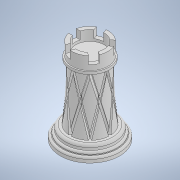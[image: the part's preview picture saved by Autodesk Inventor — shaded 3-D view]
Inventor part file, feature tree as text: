
AUTODESK INVENTOR PART (.ipt)
format: ipt  version: 2022 (Build 260153000, 153)  size: 847,872 bytes
history: native  units: mm
features: other x5, sketch x5, pattern_circular x3, loft x2, projected_geometry x2, revolve x1, extrude x1, fillet x1
ambient origin geometry x8: Origin, YZ Plane, XZ Plane, XY Plane, X Axis, Y Axis, Z Axis, Center Point
bodies: Solid1 (feature_tree)
feature tree (20):
  other  "Back Line Base.ipt"
  revolve  "Revolution1"  [1 undecoded]
  extrude  "Extrusion1"  Depth=1.0mm
  pattern_circular  "Circular Pattern1"  [2 undecoded]
  fillet  "Fillet1"  Radius=2.0mm
  sketch  "Sketch5"  dims[d4=1.0mm]
  sketch  "Sketch6"  dims[d5=0.5mm d6=7.0mm d7=2.0mm d8=2.0mm d9=360.0deg d10=1.5mm d11=1.0mm d12=3.0mm d13=3.0mm d14=0.0mm d15=50.0mm d16=360.0deg d18=1.0mm d19=4.636476mm d20=4.636476mm d21=1.0mm d22=1.0mm d23=1.0mm d24=1.0mm d25=45.0deg d42=0.0mm d43=90.0deg d44=0.0mm d45=90.0deg d46=0.0mm d47=90.0deg d48=80.0mm d49=360.0deg d51=45.0deg d52=0.1mm d53=0.1mm d54=0.0mm d55=90.0deg d56=0.0mm d57=90.0deg d58=0.0mm d59=90.0deg d60=80.0mm d61=360.0deg]
  sketch  "3D Sketch3"
  loft  "Loft4"
  loft  "Loft5"
  pattern_circular  "Circular Pattern2"  [2 undecoded]
  pattern_circular  "Circular Pattern3"  [2 undecoded]
  other  "Solid1::Back Line Base.ipt"
  other  "TaggingFeature1"
  sketch  "Sketch1"  dims[d0=10.0mm d1=30.0mm]
  projected_geometry  "Projected Loop1"
  sketch  "Sketch2"  dims[d2=5.0mm d3=1.0mm]
  projected_geometry  "Projected Loop2"
  other  "Project to Surface8"
  other  "Project to Surface9"
note: 7 required parameter values undecoded (feature->parameter linkage not recoverable at this tier; creation-order binding heuristic only, values carry confidence <= 0.55)